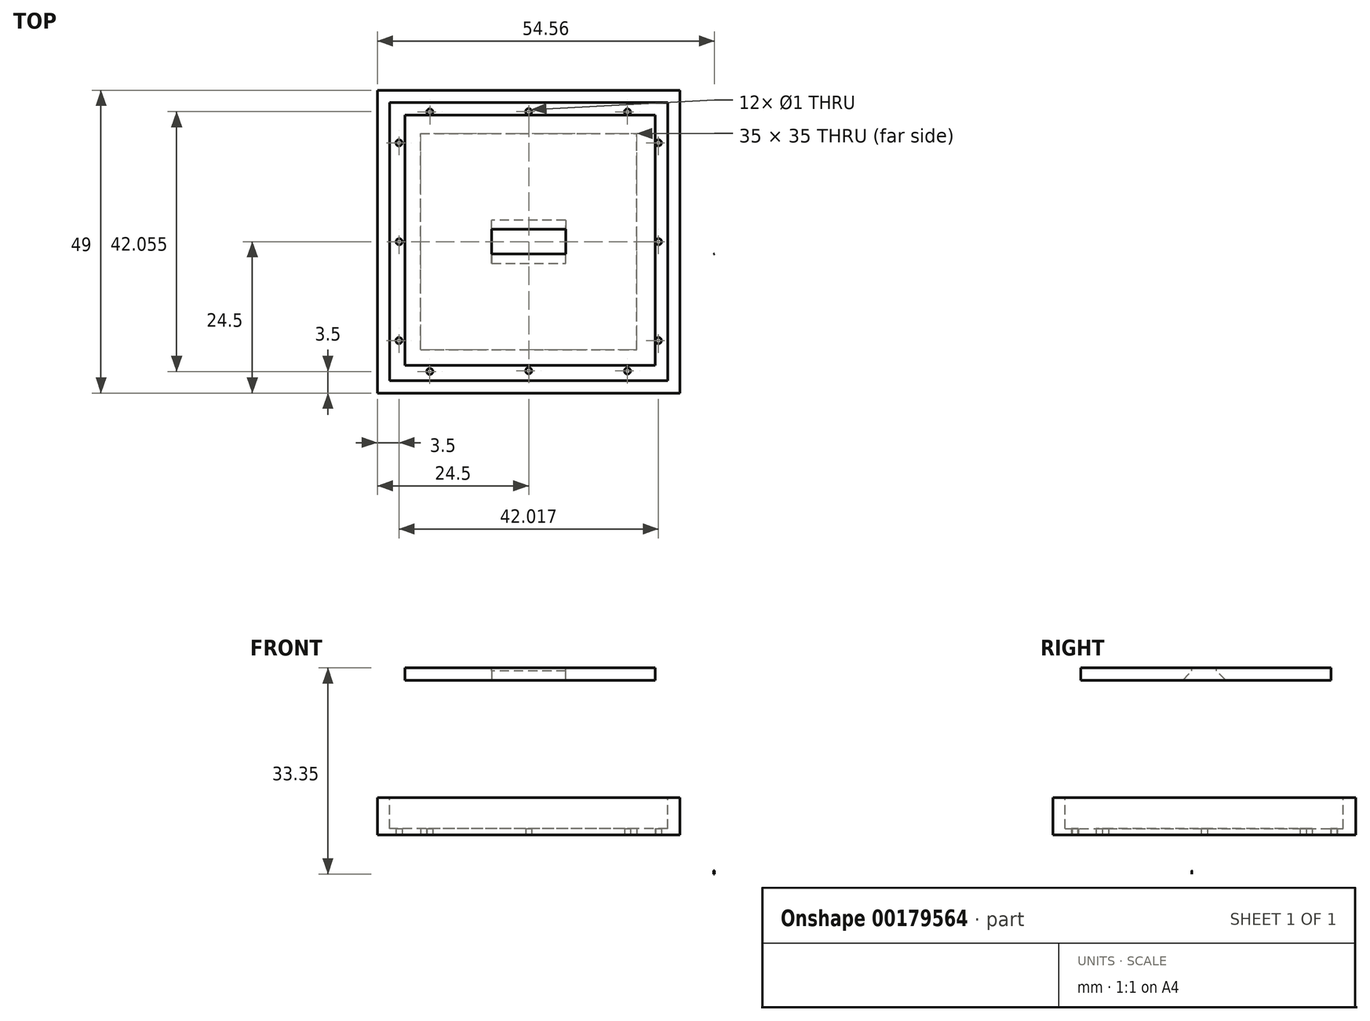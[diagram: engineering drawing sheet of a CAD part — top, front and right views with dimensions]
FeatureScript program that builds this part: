
annotation { "Feature Type Name" : "Feature", "Feature Type Description" : "" }
export const myFeature = defineFeature(function(context is Context, id is Id, definition is map)
    precondition{}
    {
        {
            var Q0;
            Q0=qCreatedBy(makeId("Top.planeOp"),FACE);
            var sketch = newSketch(context, id + "F0", { "sketchPlane" : qUnion([Q0])});
            skLineSegment(sketch, "E0.bottom", {"start": v(24.5, -24.5) * mm, "end": v(-24.5, -24.5) * mm});
            skLineSegment(sketch, "E0.top", {"start": v(24.5, 24.5) * mm, "end": v(-24.5, 24.5) * mm});
            skLineSegment(sketch, "E0.left", {"start": v(24.5, -24.5) * mm, "end": v(24.5, 24.5) * mm});
            skLineSegment(sketch, "E0.right", {"start": v(-24.5, -24.5) * mm, "end": v(-24.5, 24.5) * mm});
            skPoint(sketch, "E0.middle", {"position": v(0, 0) * mm});
            skSolve(sketch);
        }
        {
            var Q0;
            Q0=qSketchRegion(id+"F0",true);
            extrude(context, id + "F1", {"entities" : qUnion([Q0]), "depth" : 6 * mm});
        }
        {
            var Q0;
            Q0=makeQuery(id+"F1.opExtrude","CAP_FACE",FACE,{"disambiguationData":[OSD([sQuery(id+"F0.wireOp",EDGE,"E0.bottom"),sQuery(id+"F0.wireOp",EDGE,"E0.top"),sQuery(id+"F0.wireOp",EDGE,"E0.left"),sQuery(id+"F0.wireOp",EDGE,"E0.right")])],"isStart":false});
            var sketch = newSketch(context, id + "F2", { "sketchPlane" : qUnion([Q0])});
            skLineSegment(sketch, "E1.bottom", {"start": v(22.5, -22.5) * mm, "end": v(-22.5, -22.5) * mm});
            skLineSegment(sketch, "E1.top", {"start": v(22.5, 22.5) * mm, "end": v(-22.5, 22.5) * mm});
            skLineSegment(sketch, "E1.left", {"start": v(22.5, -22.5) * mm, "end": v(22.5, 22.5) * mm});
            skLineSegment(sketch, "E1.right", {"start": v(-22.5, -22.5) * mm, "end": v(-22.5, 22.5) * mm});
            skPoint(sketch, "E1.middle", {"position": v(0, 0) * mm});
            skSolve(sketch);
        }
        {
            var Q0;
            Q0=qSketchRegion(id+"F2",true);
            extrude(context, id + "F3", {"entities" : qUnion([Q0]), "operationType" : NewBodyOperationType.REMOVE, "oppositeDirection" : true, "depth" : 5 * mm});
        }
        {
            var Q0;
            Q0=makeQuery(id+"F1.opExtrude","CAP_FACE",FACE,{"disambiguationData":[OSD([sQuery(id+"F0.wireOp",EDGE,"E0.bottom"),sQuery(id+"F0.wireOp",EDGE,"E0.top"),sQuery(id+"F0.wireOp",EDGE,"E0.left"),sQuery(id+"F0.wireOp",EDGE,"E0.right")])],"isStart":true});
            var sketch = newSketch(context, id + "F4", { "sketchPlane" : qUnion([Q0])});
            skLineSegment(sketch, "E2", {"start": v(17.5, -24.5) * mm, "end": v(17.5, -17.5) * mm, "construction": true});
            skLineSegment(sketch, "E3", {"start": v(17.5, -17.5) * mm, "end": v(24.5, -17.5) * mm, "construction": true});
            skLineSegment(sketch, "E4", {"start": v(-17.5, 24.5) * mm, "end": v(-17.5, 17.5) * mm, "construction": true});
            skLineSegment(sketch, "E5", {"start": v(-17.5, 17.5) * mm, "end": v(-24.5, 17.5) * mm, "construction": true});
            skLineSegment(sketch, "E6.bottom", {"start": v(-17.5, 17.5) * mm, "end": v(17.5, 17.5) * mm});
            skLineSegment(sketch, "E6.top", {"start": v(-17.5, -17.5) * mm, "end": v(17.5, -17.5) * mm});
            skLineSegment(sketch, "E6.left", {"start": v(-17.5, 17.5) * mm, "end": v(-17.5, -17.5) * mm});
            skLineSegment(sketch, "E6.right", {"start": v(17.5, 17.5) * mm, "end": v(17.5, -17.5) * mm});
            skSolve(sketch);
        }
        {
            var Q0;
            Q0=qSketchRegion(id+"F4",true);
            extrude(context, id + "F5", {"entities" : qUnion([Q0]), "operationType" : NewBodyOperationType.REMOVE, "endBound" : BoundingType.THROUGH_ALL, "oppositeDirection" : true, "depth" : .3 * mm});
        }
        {
            var Q0;
            Q0=makeQuery(id+"F1.opExtrude","CAP_FACE",FACE,{"disambiguationData":[OSD([sQuery(id+"F0.wireOp",EDGE,"E0.bottom"),sQuery(id+"F0.wireOp",EDGE,"E0.top"),sQuery(id+"F0.wireOp",EDGE,"E0.left"),sQuery(id+"F0.wireOp",EDGE,"E0.right")])],"isStart":true});
            var sketch = newSketch(context, id + "F6", { "sketchPlane" : qUnion([Q0])});
            skLineSegment(sketch, "E7", {"start": v(17.5, 17.5) * mm, "end": v(24.5, 24.5) * mm});
            skLineSegment(sketch, "E8", {"start": v(-17.5, 17.5) * mm, "end": v(-24.5, 24.5) * mm});
            skLineSegment(sketch, "E9", {"start": v(-17.5, -17.5) * mm, "end": v(-24.5, -24.5) * mm});
            skLineSegment(sketch, "E10", {"start": v(17.5, -17.5) * mm, "end": v(24.5, -24.5) * mm});
            skLineSegment(sketch, "E11", {"start": v(-21.5, 15.5) * mm, "end": v(-21.5, -15.5) * mm, "construction": true});
            skLineSegment(sketch, "E12", {"start": v(-15.5, -21.5) * mm, "end": v(15.5, -21.5) * mm, "construction": true});
            skLineSegment(sketch, "E13", {"start": v(21.5, -15.5) * mm, "end": v(21.5, 15.5) * mm, "construction": true});
            skLineSegment(sketch, "E14", {"start": v(15.5, 21.5) * mm, "end": v(-15.5, 21.5) * mm, "construction": true});
            skSolve(sketch);
        }
        {
            var Q0;
            Q0=qCreatedBy(makeId("Right.planeOp"),FACE);
            var sketch = newSketch(context, id + "F7", { "sketchPlane" : qUnion([Q0])});
            skLineSegment(sketch, "E15", {"start": v(-2, -6.35) * mm, "end": v(-0.25, -6.35) * mm});
            skLineSegment(sketch, "E16", {"start": v(-0.25, -6.35) * mm, "end": v(-0.25, -4.35) * mm});
            skLineSegment(sketch, "E17", {"start": v(-2, -6.35) * mm, "end": v(-2, -5.85) * mm});
            skLineSegment(sketch, "E18", {"start": v(-0.5, -4.35) * mm, "end": v(-0.25, -4.35) * mm});
            skPoint(sketch, "E19.visualSharp", {"position": v(-2, -4.35) * mm});
            skArc(sketch, "E19.filletArc", {"start": v(-0.5, -4.35) * mm, "mid": v(-1.56, -4.79) * mm, "end": v(-2, -5.85) * mm});
            skSolve(sketch);
        }
        {
            var Q0;
            Q0=qSketchRegion(id+"F7",true);
            var Q1;
            Q1=qConstructionFilter(qBodyType(qCreatedBy(id+"F7",EDGE),BodyType.WIRE),ConstructionObject.NO);
            var Q2;
            Q2=sQuery(id+"F7.wireOp",EDGE,"E16");
            revolve(context, id + "F8", {"entities" : qUnion([Q0]), "surfaceEntities" : qUnion([Q1]), "axis" : qUnion([Q2]), "revolveType" : RevolveType.FULL});
        }
        {
            var Q0;
            Q0=qCreatedBy(makeId("Top.planeOp"),FACE);
            cPlane(context, id + "F9", {"entities" : qUnion([Q0]), "cplaneType" : CPlaneType.OFFSET, "offset" : 25 * mm, "width" : 150 * mm, "height" : 150 * mm});
        }
        {
            var Q0;
            Q0=qCreatedBy(id+"F9.planeOp",FACE);
            var sketch = newSketch(context, id + "F10", { "sketchPlane" : qUnion([Q0])});
            skLineSegment(sketch, "E20.bottom", {"start": v(-20.04, 20.5) * mm, "end": v(20.46, 20.5) * mm});
            skLineSegment(sketch, "E20.top", {"start": v(-20.04, -20) * mm, "end": v(20.46, -20) * mm});
            skLineSegment(sketch, "E20.left", {"start": v(-20.04, 20.5) * mm, "end": v(-20.04, -20) * mm});
            skLineSegment(sketch, "E20.right", {"start": v(20.46, 20.5) * mm, "end": v(20.46, -20) * mm});
            skSolve(sketch);
        }
        {
            var Q0;
            Q0=qSketchRegion(id+"F10",true);
            extrude(context, id + "F11", {"entities" : qUnion([Q0]), "depth" : 2 * mm});
        }
        {
            var Q0;
            Q0=makeQuery(id+"F11.opExtrude","CAP_FACE",FACE,{"disambiguationData":[OSD([sQuery(id+"F10.wireOp",EDGE,"E20.bottom"),sQuery(id+"F10.wireOp",EDGE,"E20.top"),sQuery(id+"F10.wireOp",EDGE,"E20.left"),sQuery(id+"F10.wireOp",EDGE,"E20.right")])],"isStart":false});
            var sketch = newSketch(context, id + "F12", { "sketchPlane" : qUnion([Q0])});
            skLineSegment(sketch, "E21.bottom", {"start": v(6, -2) * mm, "end": v(-6, -2) * mm});
            skLineSegment(sketch, "E21.top", {"start": v(6, 2) * mm, "end": v(-6, 2) * mm});
            skLineSegment(sketch, "E21.left", {"start": v(6, -2) * mm, "end": v(6, 2) * mm});
            skLineSegment(sketch, "E21.right", {"start": v(-6, -2) * mm, "end": v(-6, 2) * mm});
            skPoint(sketch, "E21.middle", {"position": v(0, 0) * mm});
            skSolve(sketch);
        }
        {
            var Q0;
            Q0=qSketchRegion(id+"F12",true);
            extrude(context, id + "F13", {"entities" : qUnion([Q0]), "operationType" : NewBodyOperationType.REMOVE, "endBound" : BoundingType.THROUGH_ALL, "oppositeDirection" : true, "depth" : 25 * mm});
        }
        {
            var Q0;
            Q0=makeQuery(id+"F13.boolean.opBoolean","INTERSECT",EDGE,{"derivedFrom":[makeQuery(id+"F11.opExtrude","CAP_FACE",FACE,{"disambiguationData":[OSD([sQuery(id+"F10.wireOp",EDGE,"E20.bottom"),sQuery(id+"F10.wireOp",EDGE,"E20.top"),sQuery(id+"F10.wireOp",EDGE,"E20.left"),sQuery(id+"F10.wireOp",EDGE,"E20.right")])],"isStart":true}),makeQuery(id+"F13.opExtrude","SWEPT_FACE",FACE,{"disambiguationData":[OSD([sQuery(id+"F12.wireOp",EDGE,"E21.bottom")])]})]});
            var Q1;
            Q1=makeQuery(id+"F13.boolean.opBoolean","INTERSECT",EDGE,{"derivedFrom":[makeQuery(id+"F11.opExtrude","CAP_FACE",FACE,{"disambiguationData":[OSD([sQuery(id+"F10.wireOp",EDGE,"E20.bottom"),sQuery(id+"F10.wireOp",EDGE,"E20.top"),sQuery(id+"F10.wireOp",EDGE,"E20.left"),sQuery(id+"F10.wireOp",EDGE,"E20.right")])],"isStart":true}),makeQuery(id+"F13.opExtrude","SWEPT_FACE",FACE,{"disambiguationData":[OSD([sQuery(id+"F12.wireOp",EDGE,"E21.top")])]})]});
            chamfer(context, id + "F14", {"entities" : qUnion([Q0, Q1]), "width" : 1.5 * mm, "tangentPropagation" : true});
        }
        {
            var Q0;
            Q0=makeQuery(id+"F1.opExtrude","CAP_FACE",FACE,{"disambiguationData":[OSD([sQuery(id+"F0.wireOp",EDGE,"E0.bottom"),sQuery(id+"F0.wireOp",EDGE,"E0.top"),sQuery(id+"F0.wireOp",EDGE,"E0.left"),sQuery(id+"F0.wireOp",EDGE,"E0.right")])],"isStart":true});
            var sketch = newSketch(context, id + "F15", { "sketchPlane" : qUnion([Q0])});
            skCircle(sketch, "E22", {"center": v(0, 20.9) * mm, "radius": 0.5 * mm});
            skCircle(sketch, "E23", {"center": v(-20.97, 0) * mm, "radius": 0.5 * mm});
            skCircle(sketch, "E24", {"center": v(0, -21.06) * mm, "radius": 0.5 * mm});
            skCircle(sketch, "E25", {"center": v(21.02, 0) * mm, "radius": 0.5 * mm});
            skCircle(sketch, "E26", {"center": v(21, 16) * mm, "radius": 0.5 * mm});
            skCircle(sketch, "E27", {"center": v(16, 20.92) * mm, "radius": 0.5 * mm});
            skCircle(sketch, "E28", {"center": v(-16.02, 21) * mm, "radius": 0.5 * mm});
            skCircle(sketch, "E29", {"center": v(-21, 16) * mm, "radius": 0.5 * mm});
            skCircle(sketch, "E30", {"center": v(-21, -16) * mm, "radius": 0.5 * mm});
            skCircle(sketch, "E31", {"center": v(-16, -21) * mm, "radius": 0.5 * mm});
            skCircle(sketch, "E32", {"center": v(16, -21) * mm, "radius": 0.5 * mm});
            skCircle(sketch, "E33", {"center": v(21, -16) * mm, "radius": 0.5 * mm});
            skLineSegment(sketch, "E34", {"start": v(-17.5, 16) * mm, "end": v(-24.5, 16) * mm, "construction": true});
            skLineSegment(sketch, "E35", {"start": v(-17.5, -16) * mm, "end": v(-24.5, -16) * mm, "construction": true});
            skLineSegment(sketch, "E36", {"start": v(-24.5, -16) * mm, "end": v(-24.6, -14.4) * mm, "construction": true});
            skLineSegment(sketch, "E37", {"start": v(-16, -17.5) * mm, "end": v(-16, -24.5) * mm, "construction": true});
            skLineSegment(sketch, "E38", {"start": v(16, -24.5) * mm, "end": v(16, -17.5) * mm, "construction": true});
            skLineSegment(sketch, "E39", {"start": v(17.5, -16) * mm, "end": v(24.5, -16) * mm, "construction": true});
            skLineSegment(sketch, "E40", {"start": v(17.5, 16) * mm, "end": v(24.5, 16) * mm, "construction": true});
            skLineSegment(sketch, "E41", {"start": v(16, 17.5) * mm, "end": v(16, 24.5) * mm, "construction": true});
            skLineSegment(sketch, "E42", {"start": v(-16.02, 17.5) * mm, "end": v(-16.02, 24.5) * mm, "construction": true});
            skSolve(sketch);
        }
        {
            var Q0;
            Q0=qSketchRegion(id+"F15",true);
            extrude(context, id + "F16", {"entities" : qUnion([Q0]), "operationType" : NewBodyOperationType.REMOVE, "oppositeDirection" : true, "depth" : 1 * mm});
        }
        {
            var Q0;
            Q0=makeQuery(id+"F8.opRevolve","SWEPT_BODY",BODY,{"disambiguationData":[OSD([sQuery(id+"F7.wireOp",EDGE,"ed9f9d83-8b9b-43ce-88ee-1fd96b7d1fe5"),sQuery(id+"F7.wireOp",EDGE,"E15"),sQuery(id+"F7.wireOp",EDGE,"E16")])]});
            transform(context, id + "F17", {"entities" : qUnion([Q0]), "transformType" : TransformType.TRANSLATION_3D, "dx" : 30 * mm, "dy" : 0 * mm, "dz" : 0 * mm, "makeCopy" : false});
        }
    });
